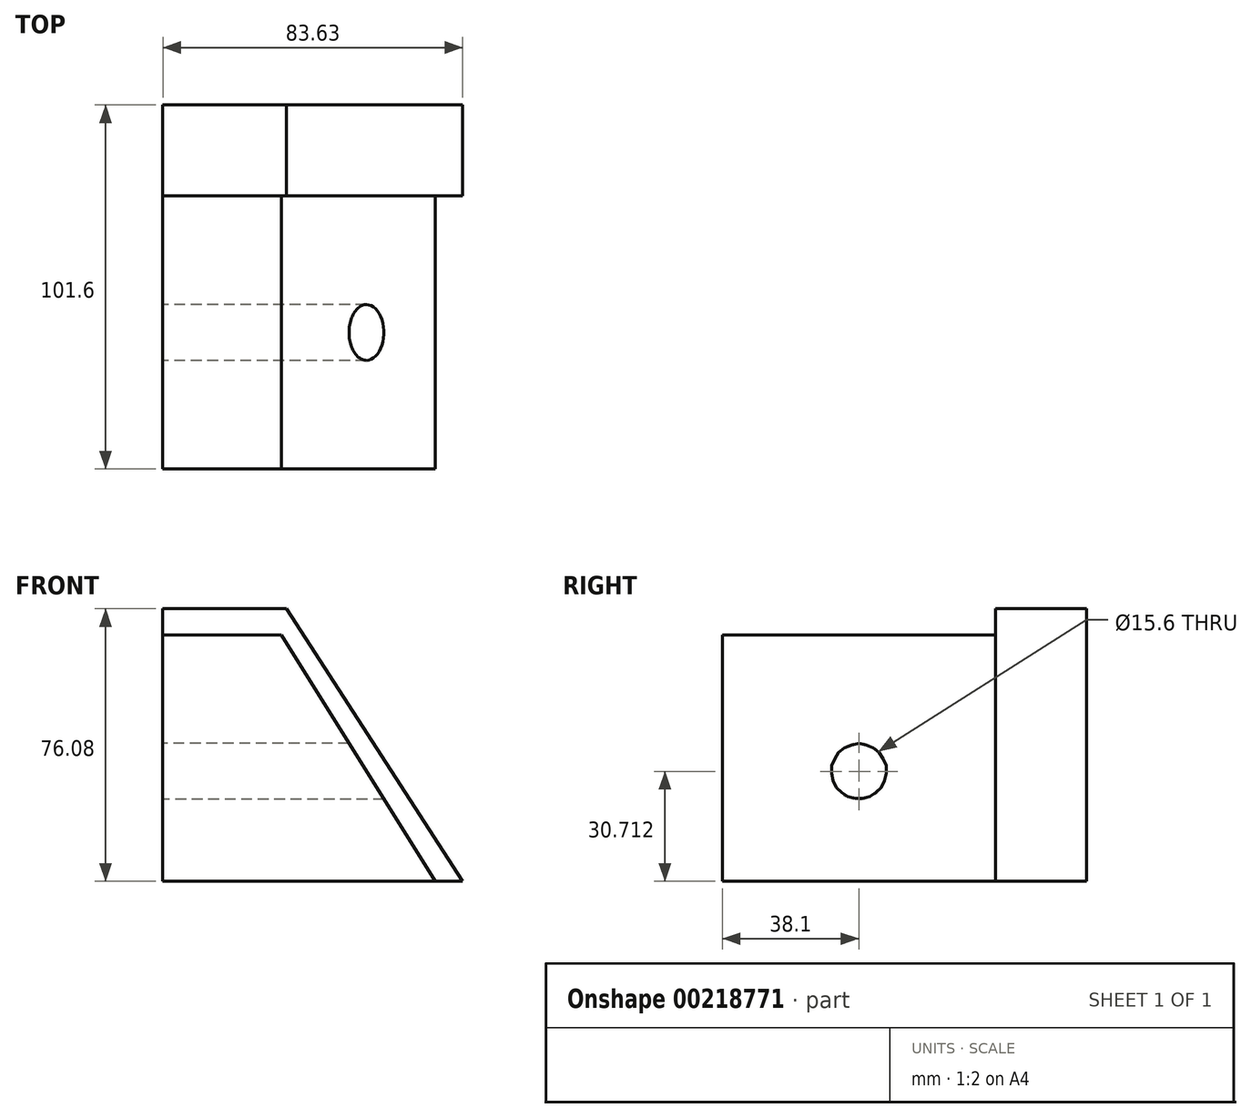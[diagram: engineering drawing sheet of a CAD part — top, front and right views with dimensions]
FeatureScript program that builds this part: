
annotation { "Feature Type Name" : "Feature", "Feature Type Description" : "" }
export const myFeature = defineFeature(function(context is Context, id is Id, definition is map)
    precondition{}
    {
        {
            var Q0;
            Q0=qCreatedBy(makeId("Front.planeOp"),FACE);
            var sketch = newSketch(context, id + "F0", { "sketchPlane" : qUnion([Q0])});
            skLineSegment(sketch, "E0", {"start": v(0, 0) * mm, "end": v(-50.38, 0) * mm});
            skLineSegment(sketch, "E1", {"start": v(-50.38, 0) * mm, "end": v(-50.38, 68.81) * mm});
            skLineSegment(sketch, "E2", {"start": v(-50.38, 68.81) * mm, "end": v(-17.34, 68.81) * mm});
            skLineSegment(sketch, "E3", {"start": v(-17.34, 68.81) * mm, "end": v(25.61, 0) * mm});
            skLineSegment(sketch, "E4", {"start": v(25.61, 0) * mm, "end": v(0, 0) * mm});
            skSolve(sketch);
        }
        {
            var Q0;
            Q0 = qSketchRegion(id + "F0", true);
            extrude(context, id + "F1", {"entities" : qUnion([Q0]), "depth" : 76.2 * mm});
        }
        {
            var Q0;
            Q0=qCreatedBy(makeId("Front.planeOp"),FACE);
            var sketch = newSketch(context, id + "F2", { "sketchPlane" : qUnion([Q0])});
            skPoint(sketch, "E5.0", {"position": v(-50.38, 68.81) * mm});
            skLineSegment(sketch, "E6.0", {"start": v(-50.38, 0) * mm, "end": v(-50.38, 68.81) * mm});
            skLineSegment(sketch, "E7", {"start": v(-50.38, 68.81) * mm, "end": v(-50.38, 76.08) * mm});
            skLineSegment(sketch, "E8", {"start": v(-50.38, 76.08) * mm, "end": v(-15.93, 76.08) * mm});
            skLineSegment(sketch, "E9", {"start": v(-15.93, 76.08) * mm, "end": v(33.25, 0) * mm});
            skLineSegment(sketch, "E10", {"start": v(33.25, 0) * mm, "end": v(-50.38, 0) * mm});
            skSolve(sketch);
        }
        {
            var Q0;
            Q0 = qSketchRegion(id + "F2", true);
            extrude(context, id + "F3", {"entities" : qUnion([Q0]), "operationType" : NewBodyOperationType.ADD, "oppositeDirection" : true, "depth" : 25.4 * mm});
        }
        {
            var Q0;
            Q0=makeQuery(id+"F3.boolean.opBoolean","MERGE",FACE,{"derivedFrom":[makeQuery(id+"F1.opExtrude","SWEPT_FACE",FACE,{"disambiguationData":[OSD([sQuery(id+"F0.wireOp",EDGE,"E1")])]}),makeQuery(id+"F3.opExtrude","SWEPT_FACE",FACE,{"disambiguationData":[OSD([sQuery(id+"F2.wireOp",EDGE,"E6.0"),sQuery(id+"F2.wireOp",EDGE,"E7")])]})]});
            var sketch = newSketch(context, id + "F4", { "sketchPlane" : qUnion([Q0])});
            skCircle(sketch, "E11", {"center": v(38.1, 30.71) * mm, "radius": 7.8 * mm});
            skSolve(sketch);
        }
        {
            var Q0;
            Q0=makeQuery(id+"F4.imprint","IMPRINT",FACE,{"disambiguationData":[TD([[makeQuery(id+"F4.imprint","IMPRINT",EDGE,{"derivedFrom":sQuery(id+"F4.wireOp",EDGE,"E11")}),1.0]])]});
            var Q1;
            Q1=sQuery(id+"F4.wireOp",EDGE,"E11");
            extrude(context, id + "F5", {"entities" : qUnion([Q0]), "operationType" : NewBodyOperationType.REMOVE, "surfaceEntities" : qUnion([Q1]), "oppositeDirection" : true, "depth" : 127 * mm});
        }
    });
